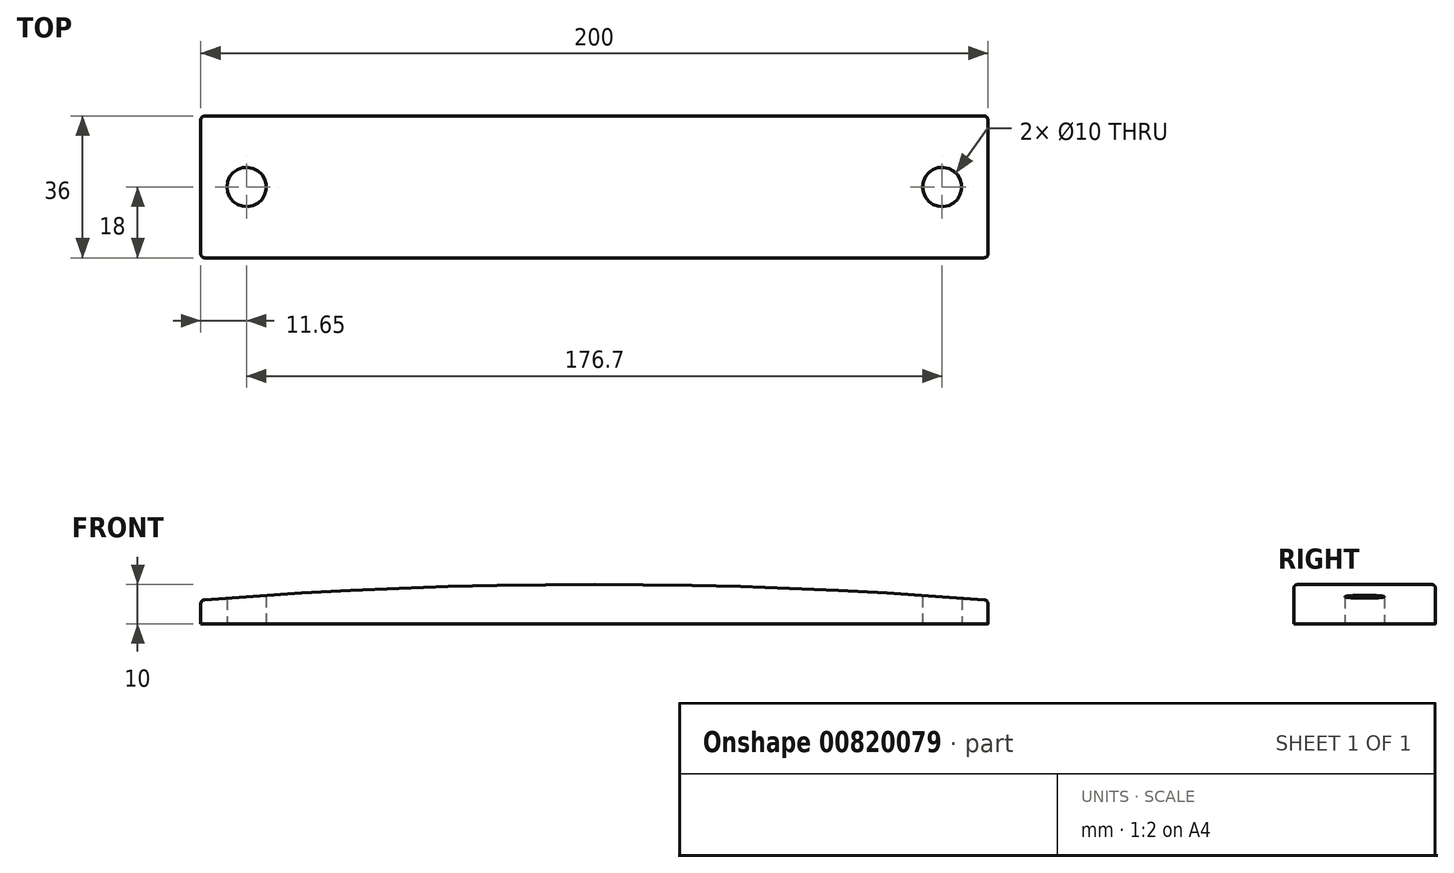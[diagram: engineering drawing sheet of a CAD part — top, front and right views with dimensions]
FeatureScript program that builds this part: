
annotation { "Feature Type Name" : "Feature", "Feature Type Description" : "" }
export const myFeature = defineFeature(function(context is Context, id is Id, definition is map)
    precondition{}
    {
        {
            var Q0;
            Q0=qCreatedBy(makeId("Front.planeOp"),FACE);
            var sketch = newSketch(context, id + "F0", { "sketchPlane" : qUnion([Q0])});
            skLineSegment(sketch, "E0", {"start": v(-100, 0) * mm, "end": v(100, 0) * mm});
            skLineSegment(sketch, "E1", {"start": v(100, 0) * mm, "end": v(100, 6) * mm});
            skLineSegment(sketch, "E2", {"start": v(-100, 0) * mm, "end": v(-100, 6) * mm});
            skLineSegment(sketch, "E3", {"start": v(-65.17, 10) * mm, "end": v(0, 10) * mm, "construction": true});
            skArc(sketch, "E4", {"start": v(100, 6) * mm, "mid": v(0, 10) * mm, "end": v(-100, 6) * mm});
            skSolve(sketch);
        }
        {
            var Q0;
            Q0=makeQuery(id+"F0.imprint","IMPRINT",FACE,{"disambiguationData":[TD([[makeQuery(id+"F0.imprint","IMPRINT",EDGE,{"derivedFrom":sQuery(id+"F0.wireOp",EDGE,"E0")}),1.0]])]});
            extrude(context, id + "F1", {"entities" : qUnion([Q0]), "depth" : 18 * mm, "offsetDistance" : 25 * mm, "hasSecondDirection" : true, "secondDirectionOppositeDirection" : true, "secondDirectionDepth" : 18 * mm});
        }
        {
            var Q0;
            Q0=qCreatedBy(makeId("Top.planeOp"),FACE);
            var sketch = newSketch(context, id + "F2", { "sketchPlane" : qUnion([Q0])});
            skCircle(sketch, "E5", {"center": v(-88.35, 0) * mm, "radius": 5 * mm});
            skCircle(sketch, "E6", {"center": v(88.35, 0) * mm, "radius": 5 * mm});
            skSolve(sketch);
        }
        {
            var Q0;
            Q0=qSketchRegion(id+"F2",true);
            extrude(context, id + "F3", {"entities" : qUnion([Q0]), "operationType" : NewBodyOperationType.REMOVE, "depth" : 25 * mm, "offsetDistance" : 25 * mm});
        }
        {
            var Q0;
            Q0=makeQuery(id+"F1.opExtrude","SWEPT_EDGE",EDGE,{"disambiguationData":[OSD([sQuery(id+"F0.wireOp",EDGE,"E2"),sQuery(id+"F0.wireOp",EDGE,"E4")])]});
            var Q1;
            Q1=makeQuery(id+"F1.opExtrude","CAP_EDGE",EDGE,{"disambiguationData":[OSD([sQuery(id+"F0.wireOp",EDGE,"E4")])],"isStart":false});
            var Q2;
            Q2=makeQuery(id+"F1.opExtrude","SWEPT_EDGE",EDGE,{"disambiguationData":[OSD([sQuery(id+"F0.wireOp",EDGE,"E1"),sQuery(id+"F0.wireOp",EDGE,"E4")])]});
            var Q3;
            Q3=makeQuery(id+"F1.opExtrude","CAP_EDGE",EDGE,{"disambiguationData":[OSD([sQuery(id+"F0.wireOp",EDGE,"E4")])],"isStart":true});
            var Q4;
            Q4=makeQuery(id+"F1.opExtrude","CAP_EDGE",EDGE,{"disambiguationData":[OSD([sQuery(id+"F0.wireOp",EDGE,"E1")])],"isStart":false});
            var Q5;
            Q5=makeQuery(id+"F1.opExtrude","CAP_EDGE",EDGE,{"disambiguationData":[OSD([sQuery(id+"F0.wireOp",EDGE,"E1")])],"isStart":true});
            var Q6;
            Q6=makeQuery(id+"F1.opExtrude","CAP_EDGE",EDGE,{"disambiguationData":[OSD([sQuery(id+"F0.wireOp",EDGE,"E2")])],"isStart":true});
            var Q7;
            Q7=makeQuery(id+"F1.opExtrude","CAP_EDGE",EDGE,{"disambiguationData":[OSD([sQuery(id+"F0.wireOp",EDGE,"E2")])],"isStart":false});
            fillet(context, id + "F4", {"entities" : qUnion([Q0, Q1, Q2, Q3, Q4, Q5, Q6, Q7]), "radius" : 1 * mm, "tangentPropagation" : true, "allowEdgeOverflow" : false});
        }
    });
